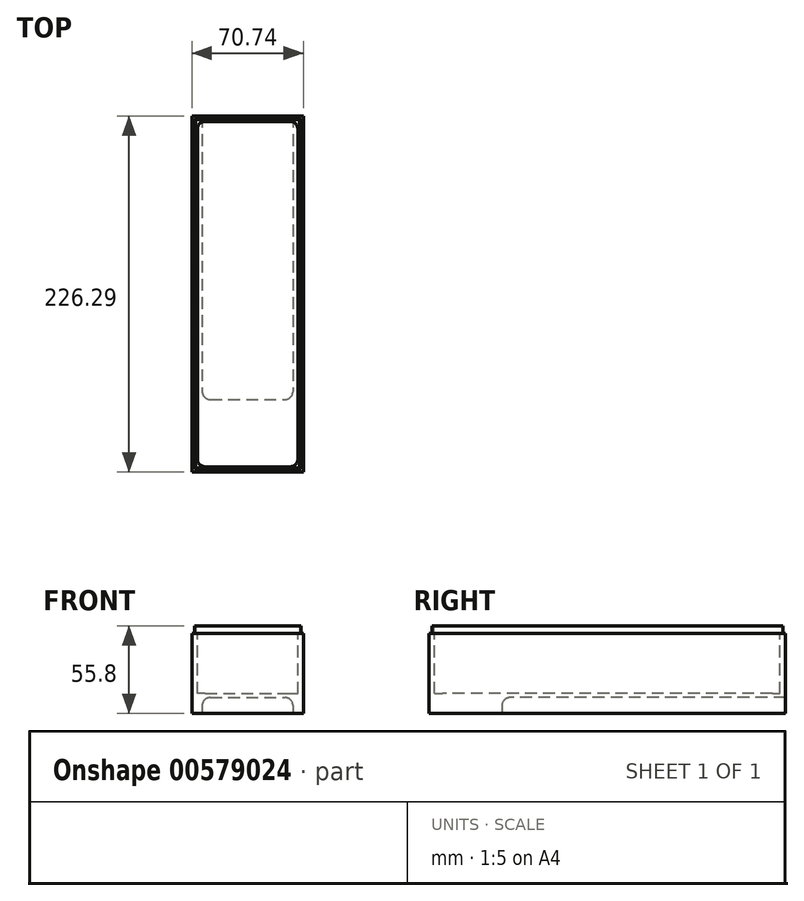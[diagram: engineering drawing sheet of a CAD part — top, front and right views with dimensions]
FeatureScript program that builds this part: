
annotation { "Feature Type Name" : "Feature", "Feature Type Description" : "" }
export const myFeature = defineFeature(function(context is Context, id is Id, definition is map)
    precondition{}
    {
        {
            var Q0;
            Q0=qCreatedBy(makeId("Top.planeOp"),FACE);
            var sketch = newSketch(context, id + "F0", { "sketchPlane" : qUnion([Q0])});
            skLineSegment(sketch, "E0.bottom", {"start": v(-43.44, 147.8) * mm, "end": v(27.3, 147.8) * mm});
            skLineSegment(sketch, "E0.top", {"start": v(-43.44, -78.48) * mm, "end": v(27.3, -78.48) * mm});
            skLineSegment(sketch, "E0.left", {"start": v(-43.44, 147.8) * mm, "end": v(-43.44, -78.48) * mm});
            skLineSegment(sketch, "E0.right", {"start": v(27.3, 147.8) * mm, "end": v(27.3, -78.48) * mm});
            skSolve(sketch);
        }
        {
            var Q0;
            Q0=makeQuery(id+"F0.imprint","IMPRINT",FACE,{"disambiguationData":[TD([[makeQuery(id+"F0.imprint","IMPRINT",EDGE,{"derivedFrom":sQuery(id+"F0.wireOp",EDGE,"E0.bottom")}),-1.0]])]});
            extrude(context, id + "F1", {"entities" : qUnion([Q0]), "depth" : 50.8 * mm, "offsetDistance" : 25.4 * mm});
        }
        {
            var Q0;
            Q0=makeQuery(id+"F1.opExtrude","CAP_FACE",FACE,{"disambiguationData":[OSD([sQuery(id+"F0.wireOp",EDGE,"E0.bottom"),sQuery(id+"F0.wireOp",EDGE,"E0.top"),sQuery(id+"F0.wireOp",EDGE,"E0.left"),sQuery(id+"F0.wireOp",EDGE,"E0.right")])],"isStart":false});
            var sketch = newSketch(context, id + "F2", { "sketchPlane" : qUnion([Q0])});
            skLineSegment(sketch, "E1.bottom", {"start": v(-39.99, 144.38) * mm, "end": v(23.84, 144.38) * mm});
            skLineSegment(sketch, "E1.top", {"start": v(-39.99, -75.05) * mm, "end": v(23.84, -75.05) * mm});
            skLineSegment(sketch, "E1.left", {"start": v(-39.99, 144.38) * mm, "end": v(-39.99, -75.05) * mm});
            skLineSegment(sketch, "E1.right", {"start": v(23.84, 144.38) * mm, "end": v(23.84, -75.05) * mm});
            skSolve(sketch);
        }
        {
            var Q0;
            Q0=makeQuery(id+"F2.imprint","IMPRINT",FACE,{"disambiguationData":[TD([[makeQuery(id+"F2.imprint","IMPRINT",EDGE,{"derivedFrom":sQuery(id+"F2.wireOp",EDGE,"E1.bottom")}),-1.0]])]});
            extrude(context, id + "F3", {"entities" : qUnion([Q0]), "operationType" : NewBodyOperationType.REMOVE, "oppositeDirection" : true, "depth" : 38.1 * mm, "offsetDistance" : 25.4 * mm});
        }
        {
            var Q0;
            Q0=makeQuery(id+"F1.opExtrude","CAP_FACE",FACE,{"disambiguationData":[OSD([sQuery(id+"F0.wireOp",EDGE,"E0.bottom"),sQuery(id+"F0.wireOp",EDGE,"E0.top"),sQuery(id+"F0.wireOp",EDGE,"E0.left"),sQuery(id+"F0.wireOp",EDGE,"E0.right")])],"isStart":true});
            var sketch = newSketch(context, id + "F4", { "sketchPlane" : qUnion([Q0])});
            skLineSegment(sketch, "E2.bottom", {"start": v(-36.86, -147.8) * mm, "end": v(20.72, -147.8) * mm});
            skLineSegment(sketch, "E2.top", {"start": v(-36.86, 32.25) * mm, "end": v(20.72, 32.25) * mm});
            skLineSegment(sketch, "E2.left", {"start": v(-36.86, -147.8) * mm, "end": v(-36.86, 32.25) * mm});
            skLineSegment(sketch, "E2.right", {"start": v(20.72, -147.8) * mm, "end": v(20.72, 32.25) * mm});
            skSolve(sketch);
        }
        {
            var Q0;
            Q0 = qSketchRegion(id + "F4", true);
            extrude(context, id + "F5", {"entities" : qUnion([Q0]), "operationType" : NewBodyOperationType.REMOVE, "oppositeDirection" : true, "depth" : 10.16 * mm, "offsetDistance" : 25.4 * mm});
        }
        {
            var Q0;
            Q0=makeQuery(id+"F5.boolean.opBoolean","COPY",EDGE,{"derivedFrom":makeQuery(id+"F5.opExtrude","CAP_EDGE",EDGE,{"disambiguationData":[OSD([sQuery(id+"F4.wireOp",EDGE,"E2.left")])],"isStart":false})});
            var Q1;
            Q1=makeQuery(id+"F5.boolean.opBoolean","COPY",EDGE,{"derivedFrom":makeQuery(id+"F5.opExtrude","CAP_EDGE",EDGE,{"disambiguationData":[OSD([sQuery(id+"F4.wireOp",EDGE,"E2.right")])],"isStart":false})});
            var Q2;
            Q2=makeQuery(id+"F5.boolean.opBoolean","COPY",EDGE,{"derivedFrom":makeQuery(id+"F5.opExtrude","CAP_EDGE",EDGE,{"disambiguationData":[OSD([sQuery(id+"F4.wireOp",EDGE,"E2.top")])],"isStart":false})});
            var Q3;
            Q3=makeQuery(id+"F5.boolean.opBoolean","COPY",EDGE,{"derivedFrom":makeQuery(id+"F5.opExtrude","SWEPT_EDGE",EDGE,{"disambiguationData":[OSD([sQuery(id+"F4.wireOp",EDGE,"E2.top"),sQuery(id+"F4.wireOp",EDGE,"E2.left")])]})});
            var Q4;
            Q4=makeQuery(id+"F5.boolean.opBoolean","COPY",EDGE,{"derivedFrom":makeQuery(id+"F5.opExtrude","SWEPT_EDGE",EDGE,{"disambiguationData":[OSD([sQuery(id+"F4.wireOp",EDGE,"E2.top"),sQuery(id+"F4.wireOp",EDGE,"E2.right")])]})});
            var Q5;
            Q5=makeQuery(id+"F3.boolean.opBoolean","COPY",EDGE,{"derivedFrom":makeQuery(id+"F3.opExtrude","SWEPT_EDGE",EDGE,{"disambiguationData":[OSD([sQuery(id+"F2.wireOp",EDGE,"E1.top"),sQuery(id+"F2.wireOp",EDGE,"E1.left")])]})});
            var Q6;
            Q6=makeQuery(id+"F3.boolean.opBoolean","COPY",EDGE,{"derivedFrom":makeQuery(id+"F3.opExtrude","SWEPT_EDGE",EDGE,{"disambiguationData":[OSD([sQuery(id+"F2.wireOp",EDGE,"E1.bottom"),sQuery(id+"F2.wireOp",EDGE,"E1.left")])]})});
            var Q7;
            Q7=makeQuery(id+"F3.boolean.opBoolean","COPY",EDGE,{"derivedFrom":makeQuery(id+"F3.opExtrude","SWEPT_EDGE",EDGE,{"disambiguationData":[OSD([sQuery(id+"F2.wireOp",EDGE,"E1.bottom"),sQuery(id+"F2.wireOp",EDGE,"E1.right")])]})});
            var Q8;
            Q8=makeQuery(id+"F3.boolean.opBoolean","COPY",EDGE,{"derivedFrom":makeQuery(id+"F3.opExtrude","SWEPT_EDGE",EDGE,{"disambiguationData":[OSD([sQuery(id+"F2.wireOp",EDGE,"E1.top"),sQuery(id+"F2.wireOp",EDGE,"E1.right")])]})});
            fillet(context, id + "F6", {"entities" : qUnion([Q0, Q1, Q2, Q3, Q4, Q5, Q6, Q7, Q8]), "radius" : 5 * mm, "tangentPropagation" : true, "allowEdgeOverflow" : false});
        }
        {
            var Q0;
            Q0=makeQuery(id+"F1.opExtrude","CAP_FACE",FACE,{"disambiguationData":[OSD([sQuery(id+"F0.wireOp",EDGE,"E0.bottom"),sQuery(id+"F0.wireOp",EDGE,"E0.top"),sQuery(id+"F0.wireOp",EDGE,"E0.left"),sQuery(id+"F0.wireOp",EDGE,"E0.right")])],"isStart":false});
            var sketch = newSketch(context, id + "F7", { "sketchPlane" : qUnion([Q0])});
            skLineSegment(sketch, "E3.bottom", {"start": v(-41.92, 146.28) * mm, "end": v(25.77, 146.28) * mm});
            skLineSegment(sketch, "E3.top", {"start": v(-41.92, -76.58) * mm, "end": v(25.77, -76.58) * mm});
            skLineSegment(sketch, "E3.left", {"start": v(-41.92, 146.28) * mm, "end": v(-41.92, -76.58) * mm});
            skLineSegment(sketch, "E3.right", {"start": v(25.77, 146.28) * mm, "end": v(25.77, -76.58) * mm});
            skLineSegment(sketch, "E4.bottom", {"start": v(-41.16, 145.52) * mm, "end": v(25, 145.52) * mm});
            skLineSegment(sketch, "E4.top", {"start": v(-41.16, -75.81) * mm, "end": v(25, -75.81) * mm});
            skLineSegment(sketch, "E4.left", {"start": v(-41.16, 145.52) * mm, "end": v(-41.16, -75.81) * mm});
            skLineSegment(sketch, "E4.right", {"start": v(25, 145.52) * mm, "end": v(25, -75.81) * mm});
            skSolve(sketch);
        }
        {
            var Q0;
            Q0 = qSketchRegion(id + "F7", true);
            extrude(context, id + "F8", {"entities" : qUnion([Q0]), "operationType" : NewBodyOperationType.ADD, "depth" : 5 * mm, "offsetDistance" : 25.4 * mm});
        }
    });
